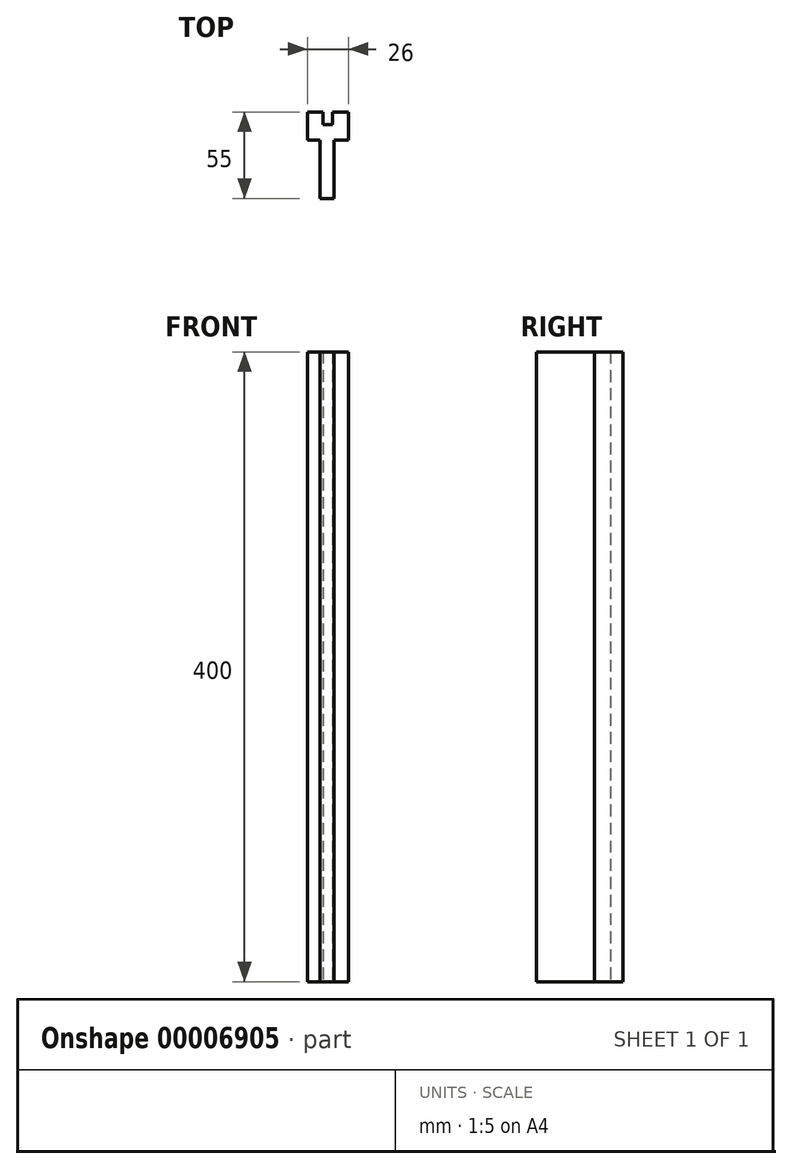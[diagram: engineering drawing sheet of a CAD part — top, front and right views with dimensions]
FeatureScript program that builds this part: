
annotation { "Feature Type Name" : "Feature", "Feature Type Description" : "" }
export const myFeature = defineFeature(function(context is Context, id is Id, definition is map)
    precondition{}
    {
        {
            var Q0;
            Q0=qCreatedBy(makeId("Top.planeOp"),FACE);
            var sketch = newSketch(context, id + "F0", { "sketchPlane" : qUnion([Q0])});
            skLineSegment(sketch, "E0.top", {"start": v(0, 47) * mm, "end": v(-25, 47) * mm});
            skLineSegment(sketch, "E1.bottom", {"start": v(-25, 47) * mm, "end": v(1, 47) * mm});
            skLineSegment(sketch, "E1.top", {"start": v(-25, 37) * mm, "end": v(1, 37) * mm});
            skLineSegment(sketch, "E1.left", {"start": v(-25, 47) * mm, "end": v(-25, 37) * mm});
            skLineSegment(sketch, "E1.right", {"start": v(1, 47) * mm, "end": v(1, 37) * mm});
            skLineSegment(sketch, "E2.bottom", {"start": v(-25, 47) * mm, "end": v(-15, 47) * mm});
            skLineSegment(sketch, "E2.top", {"start": v(-25, 55) * mm, "end": v(-15, 55) * mm});
            skLineSegment(sketch, "E2.left", {"start": v(-25, 47) * mm, "end": v(-25, 55) * mm});
            skLineSegment(sketch, "E2.right", {"start": v(-15, 47) * mm, "end": v(-15, 55) * mm});
            skLineSegment(sketch, "E3.bottom", {"start": v(1, 47) * mm, "end": v(-9, 47) * mm});
            skLineSegment(sketch, "E3.top", {"start": v(1, 55) * mm, "end": v(-9, 55) * mm});
            skLineSegment(sketch, "E3.left", {"start": v(1, 47) * mm, "end": v(1, 55) * mm});
            skLineSegment(sketch, "E3.right", {"start": v(-9, 47) * mm, "end": v(-9, 55) * mm});
            skLineSegment(sketch, "E4.bottom", {"start": v(-12, 47) * mm, "end": v(-12, 47) * mm});
            skLineSegment(sketch, "E4.top", {"start": v(-12, 37) * mm, "end": v(-12, 37) * mm});
            skLineSegment(sketch, "E4.left", {"start": v(-12, 47) * mm, "end": v(-12, 37) * mm});
            skLineSegment(sketch, "E4.right", {"start": v(-12, 47) * mm, "end": v(-12, 37) * mm});
            skLineSegment(sketch, "E5", {"start": v(-17.2, 37) * mm, "end": v(-17.2, 0) * mm});
            skLineSegment(sketch, "E6", {"start": v(-17.2, 0) * mm, "end": v(-8.13, 0) * mm});
            skLineSegment(sketch, "E7", {"start": v(-8.13, 0) * mm, "end": v(-8.13, 37) * mm});
            skSolve(sketch);
        }
        {
            var Q0;
            Q0=qSketchRegion(id+"F0",true);
            extrude(context, id + "F1", {"entities" : qUnion([Q0]), "depth" : (400) * mm});
        }
    });
